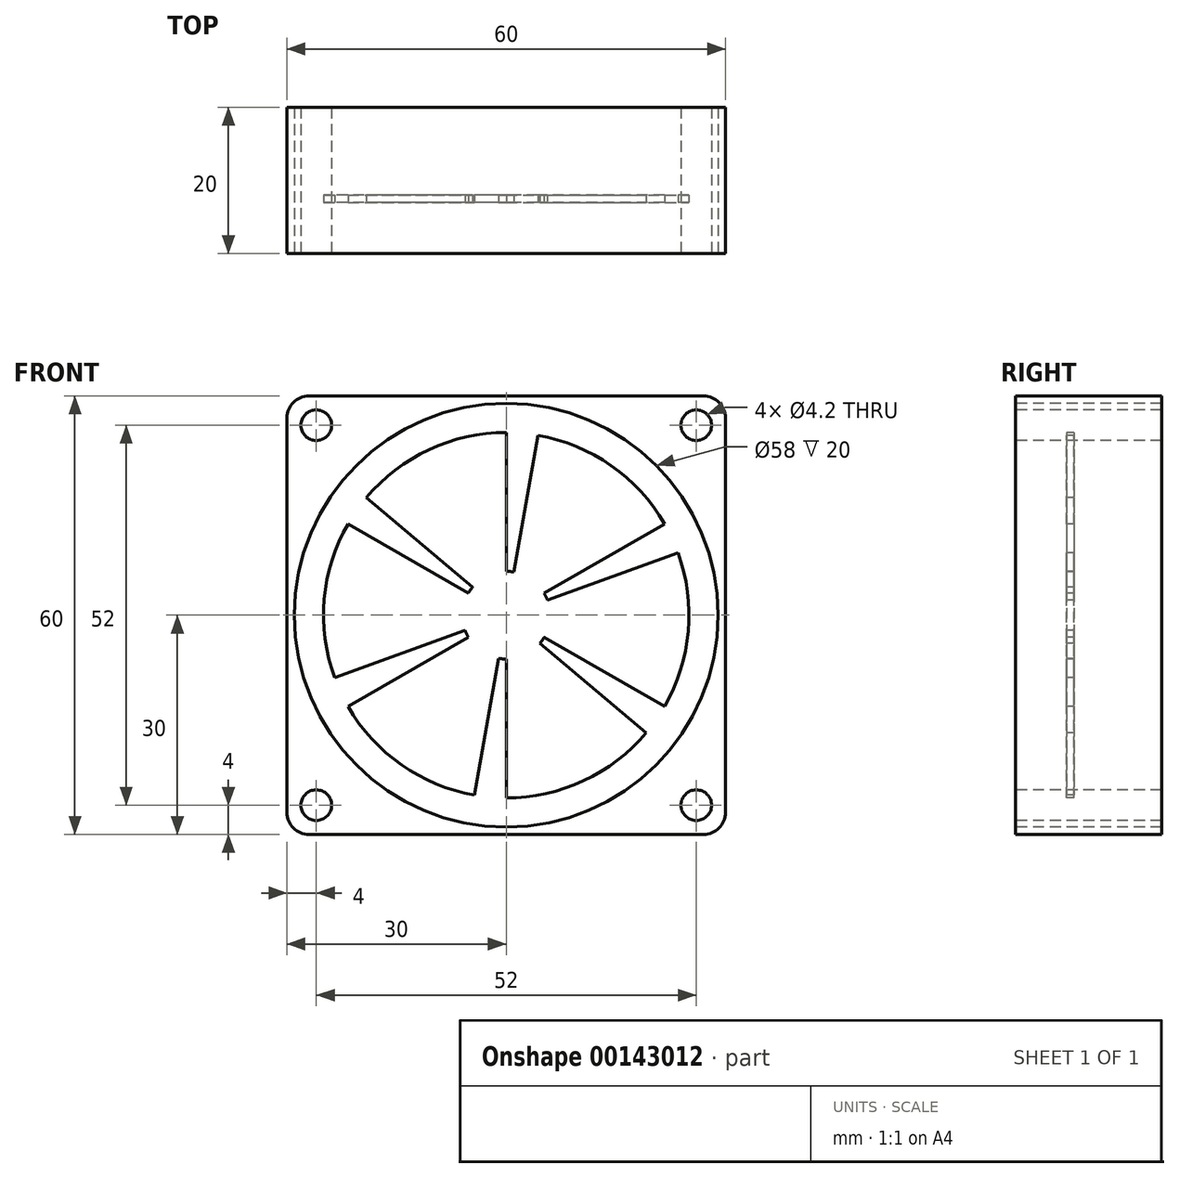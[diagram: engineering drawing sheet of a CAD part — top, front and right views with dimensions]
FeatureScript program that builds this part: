
annotation { "Feature Type Name" : "Feature", "Feature Type Description" : "" }
export const myFeature = defineFeature(function(context is Context, id is Id, definition is map)
    precondition{}
    {
        {
            var Q0;
            Q0=qCreatedBy(makeId("Front.planeOp"),FACE);
            var sketch = newSketch(context, id + "F0", { "sketchPlane" : qUnion([Q0])});
            skCircle(sketch, "E0", {"center": v(0, 0) * mm, "radius": 29 * mm});
            skCircle(sketch, "E1", {"center": v(0, 0) * mm, "radius": 25 * mm, "construction": true});
            skArc(sketch, "E2", {"start": v(0, 25) * mm, "mid": v(-10.57, 22.66) * mm, "end": v(-19.15, 16.07) * mm, "construction": true});
            skArc(sketch, "E3.1.0", {"start": v(-21.65, -12.5) * mm, "mid": v(-14.34, -20.48) * mm, "end": v(-4.34, -24.62) * mm, "construction": true});
            skArc(sketch, "E3.2.0", {"start": v(21.65, -12.5) * mm, "mid": v(24.9, -2.18) * mm, "end": v(23.5, 8.55) * mm, "construction": true});
            skArc(sketch, "E4", {"start": v(0, 25) * mm, "mid": v(-10.57, 22.66) * mm, "end": v(-19.15, 16.07) * mm});
            skCircle(sketch, "E5", {"center": v(0, 0) * mm, "radius": 6 * mm, "construction": true});
            skLineSegment(sketch, "E6", {"start": v(-19.15, 16.07) * mm, "end": v(0, 0) * mm, "construction": true});
            skLineSegment(sketch, "E7", {"start": v(0, 25) * mm, "end": v(0, 0) * mm, "construction": true});
            skLineSegment(sketch, "E8", {"start": v(0, 25) * mm, "end": v(0, 6) * mm});
            skLineSegment(sketch, "E9", {"start": v(-19.15, 16.07) * mm, "end": v(-4.6, 3.86) * mm});
            skArc(sketch, "E10", {"start": v(0, 6) * mm, "mid": v(-2.54, 5.44) * mm, "end": v(-4.6, 3.86) * mm});
            skLineSegment(sketch, "E11.1.0", {"start": v(-21.65, 12.5) * mm, "end": v(0, 0) * mm, "construction": true});
            skLineSegment(sketch, "E11.1.2", {"start": v(-23.5, -8.55) * mm, "end": v(0, 0) * mm, "construction": true});
            skArc(sketch, "E11.1.3", {"start": v(-21.65, 12.5) * mm, "mid": v(-24.9, 2.18) * mm, "end": v(-23.5, -8.55) * mm, "construction": true});
            skLineSegment(sketch, "E11.2.0", {"start": v(-21.65, -12.5) * mm, "end": v(0, 0) * mm, "construction": true});
            skLineSegment(sketch, "E11.2.2", {"start": v(-4.34, -24.62) * mm, "end": v(0, 0) * mm, "construction": true});
            skLineSegment(sketch, "E11.3.0", {"start": v(0, -25) * mm, "end": v(0, 0) * mm, "construction": true});
            skLineSegment(sketch, "E11.3.2", {"start": v(19.15, -16.07) * mm, "end": v(0, 0) * mm, "construction": true});
            skArc(sketch, "E11.3.3", {"start": v(0, -25) * mm, "mid": v(10.57, -22.66) * mm, "end": v(19.15, -16.07) * mm, "construction": true});
            skLineSegment(sketch, "E11.4.0", {"start": v(21.65, -12.5) * mm, "end": v(0, 0) * mm, "construction": true});
            skLineSegment(sketch, "E11.4.2", {"start": v(23.5, 8.55) * mm, "end": v(0, 0) * mm, "construction": true});
            skLineSegment(sketch, "E11.5.0", {"start": v(21.65, 12.5) * mm, "end": v(0, 0) * mm, "construction": true});
            skLineSegment(sketch, "E11.5.2", {"start": v(4.34, 24.62) * mm, "end": v(0, 0) * mm, "construction": true});
            skArc(sketch, "E11.5.3", {"start": v(21.65, 12.5) * mm, "mid": v(14.34, 20.48) * mm, "end": v(4.34, 24.62) * mm, "construction": true});
            skLineSegment(sketch, "E12", {"start": v(-21.65, 12.5) * mm, "end": v(-5.2, 3) * mm});
            skLineSegment(sketch, "E13", {"start": v(-5.64, -2.05) * mm, "end": v(-23.5, -8.55) * mm});
            skLineSegment(sketch, "E14", {"start": v(-21.65, -12.5) * mm, "end": v(-5.2, -3) * mm});
            skLineSegment(sketch, "E15", {"start": v(-1.04, -5.9) * mm, "end": v(-4.34, -24.62) * mm});
            skLineSegment(sketch, "E16", {"start": v(0, -25) * mm, "end": v(0, -6) * mm});
            skLineSegment(sketch, "E17", {"start": v(4.6, -3.86) * mm, "end": v(19.15, -16.07) * mm});
            skLineSegment(sketch, "E18", {"start": v(21.65, -12.5) * mm, "end": v(5.2, -3) * mm});
            skLineSegment(sketch, "E19", {"start": v(5.64, 2.05) * mm, "end": v(23.5, 8.55) * mm});
            skLineSegment(sketch, "E20", {"start": v(21.65, 12.5) * mm, "end": v(5.2, 3) * mm});
            skLineSegment(sketch, "E21", {"start": v(4.34, 24.62) * mm, "end": v(1.04, 5.9) * mm});
            skArc(sketch, "E22", {"start": v(-21.65, 12.5) * mm, "mid": v(-24.9, 2.18) * mm, "end": v(-23.5, -8.55) * mm});
            skArc(sketch, "E23", {"start": v(-21.65, -12.5) * mm, "mid": v(-14.34, -20.48) * mm, "end": v(-4.34, -24.62) * mm});
            skArc(sketch, "E24", {"start": v(0, -25) * mm, "mid": v(10.57, -22.66) * mm, "end": v(19.15, -16.07) * mm});
            skArc(sketch, "E25", {"start": v(21.65, -12.5) * mm, "mid": v(24.9, -2.18) * mm, "end": v(23.5, 8.55) * mm});
            skArc(sketch, "E26", {"start": v(21.65, 12.5) * mm, "mid": v(14.34, 20.48) * mm, "end": v(4.34, 24.62) * mm});
            skArc(sketch, "E27", {"start": v(-5.2, 3) * mm, "mid": v(-5.98, 0.52) * mm, "end": v(-5.64, -2.05) * mm});
            skArc(sketch, "E28", {"start": v(-5.2, -3) * mm, "mid": v(-3.44, -4.91) * mm, "end": v(-1.04, -5.9) * mm});
            skArc(sketch, "E29", {"start": v(0, -6) * mm, "mid": v(2.54, -5.44) * mm, "end": v(4.6, -3.86) * mm});
            skArc(sketch, "E30", {"start": v(5.2, -3) * mm, "mid": v(5.98, -0.52) * mm, "end": v(5.64, 2.05) * mm});
            skArc(sketch, "E31", {"start": v(5.2, 3) * mm, "mid": v(3.44, 4.91) * mm, "end": v(1.04, 5.9) * mm});
            skCircle(sketch, "E32", {"center": v(0, 0) * mm, "radius": 6 * mm});
            skPoint(sketch, "E33", {"position": v(30, 0) * mm});
            skPoint(sketch, "E34", {"position": v(0, 30) * mm});
            skPoint(sketch, "E35", {"position": v(-30, 0) * mm});
            skPoint(sketch, "E36", {"position": v(0, -30) * mm});
            skLineSegment(sketch, "E37", {"start": v(30, 27) * mm, "end": v(30, -27) * mm});
            skLineSegment(sketch, "E38", {"start": v(-27, 30) * mm, "end": v(27, 30) * mm});
            skLineSegment(sketch, "E39", {"start": v(-30, 27) * mm, "end": v(-30, -27) * mm});
            skLineSegment(sketch, "E40", {"start": v(27, -30) * mm, "end": v(-27, -30) * mm});
            skPoint(sketch, "E41.visualSharp", {"position": v(30, 30) * mm});
            skArc(sketch, "E41.filletArc", {"start": v(30, 27) * mm, "mid": v(29.12, 29.12) * mm, "end": v(27, 30) * mm});
            skPoint(sketch, "E42.visualSharp", {"position": v(30, -30) * mm});
            skArc(sketch, "E42.filletArc", {"start": v(27, -30) * mm, "mid": v(29.12, -29.12) * mm, "end": v(30, -27) * mm});
            skPoint(sketch, "E43.visualSharp", {"position": v(-30, -30) * mm});
            skArc(sketch, "E43.filletArc", {"start": v(-30, -27) * mm, "mid": v(-29.12, -29.12) * mm, "end": v(-27, -30) * mm});
            skPoint(sketch, "E44.visualSharp", {"position": v(-30, 30) * mm});
            skArc(sketch, "E44.filletArc", {"start": v(-27, 30) * mm, "mid": v(-29.12, 29.12) * mm, "end": v(-30, 27) * mm});
            skPoint(sketch, "E45", {"position": v(-26, 26) * mm});
            skPoint(sketch, "E46", {"position": v(26, -26) * mm});
            skPoint(sketch, "E47", {"position": v(-26, -26) * mm});
            skPoint(sketch, "E48", {"position": v(26, 26) * mm});
            skSolve(sketch);
        }
        {
            var Q0;
            {var subQ0=sQuery(id+"F0.wireOp",EDGE,"BwLgvPMj-OZC6-FQKj-CP3I-fGTAewPtjAtU");var subQ1=sQuery(id+"F0.wireOp",EDGE,"neQXV5h9-Lgpl-1t7e-PloW-8c2zd6Hxe0jc");var subQ2=makeQuery(id+"F0.imprint","INTERSECT",VERTEX,{"derivedFrom":[subQ1,subQ0]});Q0=makeQuery(id+"F0.imprint","IMPRINT",FACE,{"disambiguationData":[TD([[makeQuery(id+"F0.imprint","IMPRINT",EDGE,{"disambiguationData":[TD([[subQ2,-1.0]])],"derivedFrom":subQ1}),1.0]])]});}
            var Q1;
            {var subQ0=sQuery(id+"F0.wireOp",EDGE,"0pFcfHc8-ogLW-iNzz-0oAw-nMKrA0E6USxt");var subQ1=sQuery(id+"F0.wireOp",EDGE,"neQXV5h9-Lgpl-1t7e-PloW-8c2zd6Hxe0jc");var subQ2=makeQuery(id+"F0.imprint","INTERSECT",VERTEX,{"derivedFrom":[subQ1,subQ0]});Q1=makeQuery(id+"F0.imprint","IMPRINT",FACE,{"disambiguationData":[TD([[makeQuery(id+"F0.imprint","IMPRINT",EDGE,{"disambiguationData":[TD([[subQ2,-1.0]])],"derivedFrom":subQ1}),1.0]])]});}
            var Q2;
            {var subQ0=sQuery(id+"F0.wireOp",EDGE,"MIZtZY80-euQ6-Yu8p-12dk-afmEVnUx2k1d");var subQ1=sQuery(id+"F0.wireOp",EDGE,"neQXV5h9-Lgpl-1t7e-PloW-8c2zd6Hxe0jc");var subQ2=makeQuery(id+"F0.imprint","INTERSECT",VERTEX,{"derivedFrom":[subQ1,subQ0]});Q2=makeQuery(id+"F0.imprint","IMPRINT",FACE,{"disambiguationData":[TD([[makeQuery(id+"F0.imprint","IMPRINT",EDGE,{"disambiguationData":[TD([[subQ2,-1.0]])],"derivedFrom":subQ1}),1.0]])]});}
            var Q3;
            {var subQ0=sQuery(id+"F0.wireOp",EDGE,"PsTB3vRL-USYk-gMsV-1mZ8-qJGdW2Rqm2Ei");var subQ1=sQuery(id+"F0.wireOp",EDGE,"neQXV5h9-Lgpl-1t7e-PloW-8c2zd6Hxe0jc");var subQ2=makeQuery(id+"F0.imprint","INTERSECT",VERTEX,{"derivedFrom":[subQ1,subQ0]});Q3=makeQuery(id+"F0.imprint","IMPRINT",FACE,{"disambiguationData":[TD([[makeQuery(id+"F0.imprint","IMPRINT",EDGE,{"disambiguationData":[TD([[subQ2,-1.0]])],"derivedFrom":subQ1}),1.0]])]});}
            var Q4;
            {var subQ0=sQuery(id+"F0.wireOp",EDGE,"KKMzZtHq-8PO1-tPsO-ZLri-1ZjVtMehvnvk");var subQ1=sQuery(id+"F0.wireOp",EDGE,"neQXV5h9-Lgpl-1t7e-PloW-8c2zd6Hxe0jc");var subQ2=makeQuery(id+"F0.imprint","INTERSECT",VERTEX,{"derivedFrom":[subQ1,subQ0]});Q4=makeQuery(id+"F0.imprint","IMPRINT",FACE,{"disambiguationData":[TD([[makeQuery(id+"F0.imprint","IMPRINT",EDGE,{"disambiguationData":[TD([[subQ2,-1.0]])],"derivedFrom":subQ1}),1.0]])]});}
            var Q5;
            {var subQ0=sQuery(id+"F0.wireOp",EDGE,"l8tg03Lw-Hr9p-BUbB-HZQX-xL2uWBpcb38l");var subQ1=sQuery(id+"F0.wireOp",EDGE,"neQXV5h9-Lgpl-1t7e-PloW-8c2zd6Hxe0jc");var subQ2=makeQuery(id+"F0.imprint","INTERSECT",VERTEX,{"derivedFrom":[subQ1,subQ0]});Q5=makeQuery(id+"F0.imprint","IMPRINT",FACE,{"disambiguationData":[TD([[makeQuery(id+"F0.imprint","IMPRINT",EDGE,{"disambiguationData":[TD([[subQ2,-1.0]])],"derivedFrom":subQ1}),1.0]])]});}
            var Q6;
            {var subQ0=sQuery(id+"F0.wireOp",EDGE,"rTUeonmu-QQDE-d3Li-ZIzy-7ngGtiIJYAng");var subQ1=sQuery(id+"F0.wireOp",EDGE,"neQXV5h9-Lgpl-1t7e-PloW-8c2zd6Hxe0jc");var subQ2=makeQuery(id+"F0.imprint","INTERSECT",VERTEX,{"derivedFrom":[subQ1,subQ0]});Q6=makeQuery(id+"F0.imprint","IMPRINT",FACE,{"disambiguationData":[TD([[makeQuery(id+"F0.imprint","IMPRINT",EDGE,{"disambiguationData":[TD([[subQ2,-1.0]])],"derivedFrom":subQ1}),1.0]])]});}
            var Q7;
            {var subQ0=sQuery(id+"F0.wireOp",EDGE,"nssdje4S-cbI0-p24k-TOdf-2WUK18LDSgnL");var subQ1=sQuery(id+"F0.wireOp",EDGE,"neQXV5h9-Lgpl-1t7e-PloW-8c2zd6Hxe0jc");var subQ2=makeQuery(id+"F0.imprint","INTERSECT",VERTEX,{"derivedFrom":[subQ1,subQ0]});Q7=makeQuery(id+"F0.imprint","IMPRINT",FACE,{"disambiguationData":[TD([[makeQuery(id+"F0.imprint","IMPRINT",EDGE,{"disambiguationData":[TD([[subQ2,-1.0]])],"derivedFrom":subQ1}),1.0]])]});}
            var Q8;
            {var subQ0=sQuery(id+"F0.wireOp",EDGE,"KjxKVayg-KjCi-Kcam-8UEm-DqkqyzutvIX6");var subQ1=sQuery(id+"F0.wireOp",EDGE,"neQXV5h9-Lgpl-1t7e-PloW-8c2zd6Hxe0jc");var subQ2=makeQuery(id+"F0.imprint","INTERSECT",VERTEX,{"derivedFrom":[subQ1,subQ0]});Q8=makeQuery(id+"F0.imprint","IMPRINT",FACE,{"disambiguationData":[TD([[makeQuery(id+"F0.imprint","IMPRINT",EDGE,{"disambiguationData":[TD([[subQ2,-1.0]])],"derivedFrom":subQ1}),1.0]])]});}
            var Q9;
            {var subQ0=sQuery(id+"F0.wireOp",EDGE,"KjxKVayg-KjCi-Kcam-8UEm-DqkqyzutvIX6");var subQ1=sQuery(id+"F0.wireOp",EDGE,"neQXV5h9-Lgpl-1t7e-PloW-8c2zd6Hxe0jc");var subQ2=makeQuery(id+"F0.imprint","INTERSECT",VERTEX,{"derivedFrom":[subQ1,subQ0]});Q9=makeQuery(id+"F0.imprint","IMPRINT",FACE,{"disambiguationData":[TD([[makeQuery(id+"F0.imprint","IMPRINT",EDGE,{"disambiguationData":[TD([[subQ2,1.0]])],"derivedFrom":subQ1}),1.0]])]});}
            var Q10;
            {var subQ0=sQuery(id+"F0.wireOp",EDGE,"bUYQiRjo-FacI-MEWE-HjEw-WaeuQtsQwpRp");var subQ1=sQuery(id+"F0.wireOp",EDGE,"neQXV5h9-Lgpl-1t7e-PloW-8c2zd6Hxe0jc");var subQ2=makeQuery(id+"F0.imprint","INTERSECT",VERTEX,{"derivedFrom":[subQ1,subQ0]});Q10=makeQuery(id+"F0.imprint","IMPRINT",FACE,{"disambiguationData":[TD([[makeQuery(id+"F0.imprint","IMPRINT",EDGE,{"disambiguationData":[TD([[subQ2,1.0]])],"derivedFrom":subQ1}),1.0]])]});}
            var Q11;
            {var subQ0=sQuery(id+"F0.wireOp",EDGE,"SQEkTNfe-2des-rSFJ-dj0n-PeRD2lnSvIcU");var subQ1=sQuery(id+"F0.wireOp",EDGE,"neQXV5h9-Lgpl-1t7e-PloW-8c2zd6Hxe0jc");var subQ2=makeQuery(id+"F0.imprint","INTERSECT",VERTEX,{"derivedFrom":[subQ1,subQ0]});Q11=makeQuery(id+"F0.imprint","IMPRINT",FACE,{"disambiguationData":[TD([[makeQuery(id+"F0.imprint","IMPRINT",EDGE,{"disambiguationData":[TD([[subQ2,-1.0]])],"derivedFrom":subQ1}),1.0]])]});}
            var Q12;
            {var subQ0=sQuery(id+"F0.wireOp",EDGE,"TIu3GGqD-eKRK-YzJF-ymvG-cx5AxaY1HUlY");var subQ1=sQuery(id+"F0.wireOp",EDGE,"neQXV5h9-Lgpl-1t7e-PloW-8c2zd6Hxe0jc");var subQ2=makeQuery(id+"F0.imprint","INTERSECT",VERTEX,{"derivedFrom":[subQ1,subQ0]});Q12=makeQuery(id+"F0.imprint","IMPRINT",FACE,{"disambiguationData":[TD([[makeQuery(id+"F0.imprint","IMPRINT",EDGE,{"disambiguationData":[TD([[subQ2,-1.0]])],"derivedFrom":subQ1}),1.0]])]});}
            var Q13;
            {var subQ0=sQuery(id+"F0.wireOp",EDGE,"Cg44zFhS-ptB2-BMPP-LHXV-p0LVbA2ra7Ie");var subQ1=sQuery(id+"F0.wireOp",EDGE,"neQXV5h9-Lgpl-1t7e-PloW-8c2zd6Hxe0jc");var subQ2=makeQuery(id+"F0.imprint","INTERSECT",VERTEX,{"derivedFrom":[subQ1,subQ0]});Q13=makeQuery(id+"F0.imprint","IMPRINT",FACE,{"disambiguationData":[TD([[makeQuery(id+"F0.imprint","IMPRINT",EDGE,{"disambiguationData":[TD([[subQ2,-1.0]])],"derivedFrom":subQ1}),1.0]])]});}
            var Q14;
            {var subQ0=sQuery(id+"F0.wireOp",EDGE,"HYAgJyV6-WnQI-W0wT-IZif-ZUp3knaBoTfx");var subQ1=sQuery(id+"F0.wireOp",EDGE,"neQXV5h9-Lgpl-1t7e-PloW-8c2zd6Hxe0jc");var subQ2=makeQuery(id+"F0.imprint","INTERSECT",VERTEX,{"derivedFrom":[subQ1,subQ0]});Q14=makeQuery(id+"F0.imprint","IMPRINT",FACE,{"disambiguationData":[TD([[makeQuery(id+"F0.imprint","IMPRINT",EDGE,{"disambiguationData":[TD([[subQ2,-1.0]])],"derivedFrom":subQ1}),1.0]])]});}
            var Q15;
            {var subQ0=sQuery(id+"F0.wireOp",EDGE,"dE4ENxce-THc3-QNUE-QZnd-ZCCbtDuI6Ybd");var subQ1=sQuery(id+"F0.wireOp",EDGE,"neQXV5h9-Lgpl-1t7e-PloW-8c2zd6Hxe0jc");var subQ2=makeQuery(id+"F0.imprint","INTERSECT",VERTEX,{"derivedFrom":[subQ1,subQ0]});Q15=makeQuery(id+"F0.imprint","IMPRINT",FACE,{"disambiguationData":[TD([[makeQuery(id+"F0.imprint","IMPRINT",EDGE,{"disambiguationData":[TD([[subQ2,-1.0]])],"derivedFrom":subQ1}),1.0]])]});}
            var Q16;
            {var subQ0=sQuery(id+"F0.wireOp",EDGE,"KKMzZtHq-8PO1-tPsO-ZLri-1ZjVtMehvnvk");var subQ1=sQuery(id+"F0.wireOp",EDGE,"E1");var subQ2=makeQuery(id+"F0.imprint","INTERSECT",VERTEX,{"derivedFrom":[subQ1,subQ0]});Q16=makeQuery(id+"F0.imprint","IMPRINT",FACE,{"disambiguationData":[TD([[makeQuery(id+"F0.imprint","IMPRINT",EDGE,{"disambiguationData":[TD([[subQ2,-1.0]])],"derivedFrom":subQ1}),1.0]])]});}
            var Q17;
            {var subQ0=sQuery(id+"F0.wireOp",EDGE,"KjxKVayg-KjCi-Kcam-8UEm-DqkqyzutvIX6");var subQ1=sQuery(id+"F0.wireOp",EDGE,"E1");var subQ2=makeQuery(id+"F0.imprint","INTERSECT",VERTEX,{"derivedFrom":[subQ1,subQ0]});Q17=makeQuery(id+"F0.imprint","IMPRINT",FACE,{"disambiguationData":[TD([[makeQuery(id+"F0.imprint","IMPRINT",EDGE,{"disambiguationData":[TD([[subQ2,-1.0]])],"derivedFrom":subQ1}),1.0]])]});}
            var Q18;
            {var subQ0=sQuery(id+"F0.wireOp",EDGE,"TIu3GGqD-eKRK-YzJF-ymvG-cx5AxaY1HUlY");var subQ1=sQuery(id+"F0.wireOp",EDGE,"E1");var subQ2=makeQuery(id+"F0.imprint","INTERSECT",VERTEX,{"derivedFrom":[subQ1,subQ0]});Q18=makeQuery(id+"F0.imprint","IMPRINT",FACE,{"disambiguationData":[TD([[makeQuery(id+"F0.imprint","IMPRINT",EDGE,{"disambiguationData":[TD([[subQ2,-1.0]])],"derivedFrom":subQ1}),1.0]])]});}
            var Q19;
            {var subQ0=sQuery(id+"F0.wireOp",EDGE,"BwLgvPMj-OZC6-FQKj-CP3I-fGTAewPtjAtU");var subQ1=sQuery(id+"F0.wireOp",EDGE,"E1");var subQ2=makeQuery(id+"F0.imprint","INTERSECT",VERTEX,{"derivedFrom":[subQ1,subQ0]});Q19=makeQuery(id+"F0.imprint","IMPRINT",FACE,{"disambiguationData":[TD([[makeQuery(id+"F0.imprint","IMPRINT",EDGE,{"disambiguationData":[TD([[subQ2,-1.0]])],"derivedFrom":subQ1}),1.0]])]});}
            var Q20;
            {var subQ0=sQuery(id+"F0.wireOp",EDGE,"PsTB3vRL-USYk-gMsV-1mZ8-qJGdW2Rqm2Ei");var subQ1=sQuery(id+"F0.wireOp",EDGE,"E1");var subQ2=makeQuery(id+"F0.imprint","INTERSECT",VERTEX,{"derivedFrom":[subQ1,subQ0]});Q20=makeQuery(id+"F0.imprint","IMPRINT",FACE,{"disambiguationData":[TD([[makeQuery(id+"F0.imprint","IMPRINT",EDGE,{"disambiguationData":[TD([[subQ2,-1.0]])],"derivedFrom":subQ1}),1.0]])]});}
            var Q21;
            {var subQ0=sQuery(id+"F0.wireOp",EDGE,"dE4ENxce-THc3-QNUE-QZnd-ZCCbtDuI6Ybd");var subQ1=sQuery(id+"F0.wireOp",EDGE,"E1");var subQ2=makeQuery(id+"F0.imprint","INTERSECT",VERTEX,{"derivedFrom":[subQ1,subQ0]});Q21=makeQuery(id+"F0.imprint","IMPRINT",FACE,{"disambiguationData":[TD([[makeQuery(id+"F0.imprint","IMPRINT",EDGE,{"disambiguationData":[TD([[subQ2,-1.0]])],"derivedFrom":subQ1}),1.0]])]});}
            var Q22;
            {var subQ0=sQuery(id+"F0.wireOp",EDGE,"SQEkTNfe-2des-rSFJ-dj0n-PeRD2lnSvIcU");var subQ1=sQuery(id+"F0.wireOp",EDGE,"E1");var subQ2=makeQuery(id+"F0.imprint","INTERSECT",VERTEX,{"derivedFrom":[subQ1,subQ0]});Q22=makeQuery(id+"F0.imprint","IMPRINT",FACE,{"disambiguationData":[TD([[makeQuery(id+"F0.imprint","IMPRINT",EDGE,{"disambiguationData":[TD([[subQ2,-1.0]])],"derivedFrom":subQ1}),1.0]])]});}
            var Q23;
            {var subQ0=sQuery(id+"F0.wireOp",EDGE,"nssdje4S-cbI0-p24k-TOdf-2WUK18LDSgnL");var subQ1=sQuery(id+"F0.wireOp",EDGE,"E1");var subQ2=makeQuery(id+"F0.imprint","INTERSECT",VERTEX,{"derivedFrom":[subQ1,subQ0]});Q23=makeQuery(id+"F0.imprint","IMPRINT",FACE,{"disambiguationData":[TD([[makeQuery(id+"F0.imprint","IMPRINT",EDGE,{"disambiguationData":[TD([[subQ2,-1.0]])],"derivedFrom":subQ1}),1.0]])]});}
            var Q24;
            {var subQ0=sQuery(id+"F0.wireOp",EDGE,"E20");Q24=makeQuery(id+"F0.imprint","IMPRINT",FACE,{"disambiguationData":[TD([[makeQuery(id+"F0.imprint","IMPRINT",EDGE,{"derivedFrom":subQ0}),-1.0]])]});}
            var Q25;
            {var subQ0=sQuery(id+"F0.wireOp",EDGE,"E32");var subQ8=makeQuery(id+"F0.imprint","INTERSECT",VERTEX,{"derivedFrom":[sQuery(id+"F0.wireOp",EDGE,"E19"),subQ0]});Q25=makeQuery(id+"F0.imprint","IMPRINT",FACE,{"disambiguationData":[TD([[makeQuery(id+"F0.imprint","IMPRINT",EDGE,{"disambiguationData":[TD([[subQ8,-1.0]])],"derivedFrom":subQ0}),1.0]])]});}
            var Q26;
            Q26=makeQuery(id+"F0.imprint","IMPRINT",FACE,{"disambiguationData":[TD([[makeQuery(id+"F0.imprint","IMPRINT",EDGE,{"derivedFrom":sQuery(id+"F0.wireOp",EDGE,"E4")}),1.0]])]});
            var Q27;
            {var subQ0=sQuery(id+"F0.wireOp",EDGE,"E12");Q27=makeQuery(id+"F0.imprint","IMPRINT",FACE,{"disambiguationData":[TD([[makeQuery(id+"F0.imprint","IMPRINT",EDGE,{"derivedFrom":subQ0}),-1.0]])]});}
            var Q28;
            {var subQ0=sQuery(id+"F0.wireOp",EDGE,"E14");Q28=makeQuery(id+"F0.imprint","IMPRINT",FACE,{"disambiguationData":[TD([[makeQuery(id+"F0.imprint","IMPRINT",EDGE,{"derivedFrom":subQ0}),-1.0]])]});}
            var Q29;
            {var subQ0=sQuery(id+"F0.wireOp",EDGE,"E16");Q29=makeQuery(id+"F0.imprint","IMPRINT",FACE,{"disambiguationData":[TD([[makeQuery(id+"F0.imprint","IMPRINT",EDGE,{"derivedFrom":subQ0}),-1.0]])]});}
            var Q30;
            {var subQ0=sQuery(id+"F0.wireOp",EDGE,"E18");Q30=makeQuery(id+"F0.imprint","IMPRINT",FACE,{"disambiguationData":[TD([[makeQuery(id+"F0.imprint","IMPRINT",EDGE,{"derivedFrom":subQ0}),-1.0]])]});}
            extrude(context, id + "F1", {"entities" : qUnion([Q0, Q1, Q2, Q3, Q4, Q5, Q6, Q7, Q8, Q9, Q10, Q11, Q12, Q13, Q14, Q15, Q16, Q17, Q18, Q19, Q20, Q21, Q22, Q23, Q24, Q25, Q26, Q27, Q28, Q29, Q30]), "oppositeDirection" : true, "depth" : 8 * mm, "hasSecondDirection" : true, "secondDirectionOppositeDirection" : false, "secondDirectionDepth" : -7 * mm, "offsetDistance" : 25 * mm});
        }
        {
            var Q0;
            Q0=makeQuery(id+"F0.imprint","IMPRINT",FACE,{"disambiguationData":[TD([[makeQuery(id+"F0.imprint","IMPRINT",EDGE,{"derivedFrom":sQuery(id+"F0.wireOp",EDGE,"E0")}),-1.0]])]});
            extrude(context, id + "F2", {"entities" : qUnion([Q0]), "oppositeDirection" : true, "depth" : 20 * mm, "offsetDistance" : 25 * mm});
        }
        {
            var Q0;
            Q0=sQuery(id+"F0.wireOp",VERTEX,"E45");
            var Q1;
            Q1=sQuery(id+"F0.wireOp",VERTEX,"E48");
            var Q2;
            Q2=sQuery(id+"F0.wireOp",VERTEX,"E46");
            var Q3;
            Q3=sQuery(id+"F0.wireOp",VERTEX,"E47");
            var Q4;
            Q4=makeQuery(id+"F2.opExtrude","SWEPT_BODY",BODY,{"disambiguationData":[OSD([sQuery(id+"F0.wireOp",EDGE,"E0"),sQuery(id+"F0.wireOp",EDGE,"E38"),sQuery(id+"F0.wireOp",EDGE,"E39"),sQuery(id+"F0.wireOp",EDGE,"E44.filletArc")])]});
            var Q5;
            Q5=makeQuery(id+"F2.opExtrude","SWEPT_BODY",BODY,{"disambiguationData":[OSD([sQuery(id+"F0.wireOp",EDGE,"E0"),sQuery(id+"F0.wireOp",EDGE,"E37"),sQuery(id+"F0.wireOp",EDGE,"E38"),sQuery(id+"F0.wireOp",EDGE,"E41.filletArc")])]});
            var Q6;
            Q6=makeQuery(id+"F2.opExtrude","SWEPT_BODY",BODY,{"disambiguationData":[OSD([sQuery(id+"F0.wireOp",EDGE,"E0"),sQuery(id+"F0.wireOp",EDGE,"E37"),sQuery(id+"F0.wireOp",EDGE,"E40"),sQuery(id+"F0.wireOp",EDGE,"E42.filletArc")])]});
            var Q7;
            Q7=makeQuery(id+"F2.opExtrude","SWEPT_BODY",BODY,{"disambiguationData":[OSD([sQuery(id+"F0.wireOp",EDGE,"E0"),sQuery(id+"F0.wireOp",EDGE,"E39"),sQuery(id+"F0.wireOp",EDGE,"E40"),sQuery(id+"F0.wireOp",EDGE,"E43.filletArc")])]});
            hole(context, id + "F3", {"style" : HoleStyle.SIMPLE, "endStyle" : HoleEndStyle.THROUGH, "standardTappedOrClearance" : lookupTablePath({ "standard" : "ISO", "fit" : "Close", "size" : "M4", "type" : "Clearance" }), "standardBlindInLast" : lookupTablePath({ "fit" : "Close", "standard" : "ISO", "size" : "M4", "type" : "Clearance" }), "holeDiameter" : 4.2 * mm, "majorDiameter" : 5 * mm, "isTappedThrough" : true, "tappedDepth" : 12 * mm, "tapClearance" : 3, "startFromSketch" : true, "locations" : qUnion([Q0, Q1, Q2, Q3]), "scope" : qUnion([Q4, Q5, Q6, Q7])});
        }
    });
